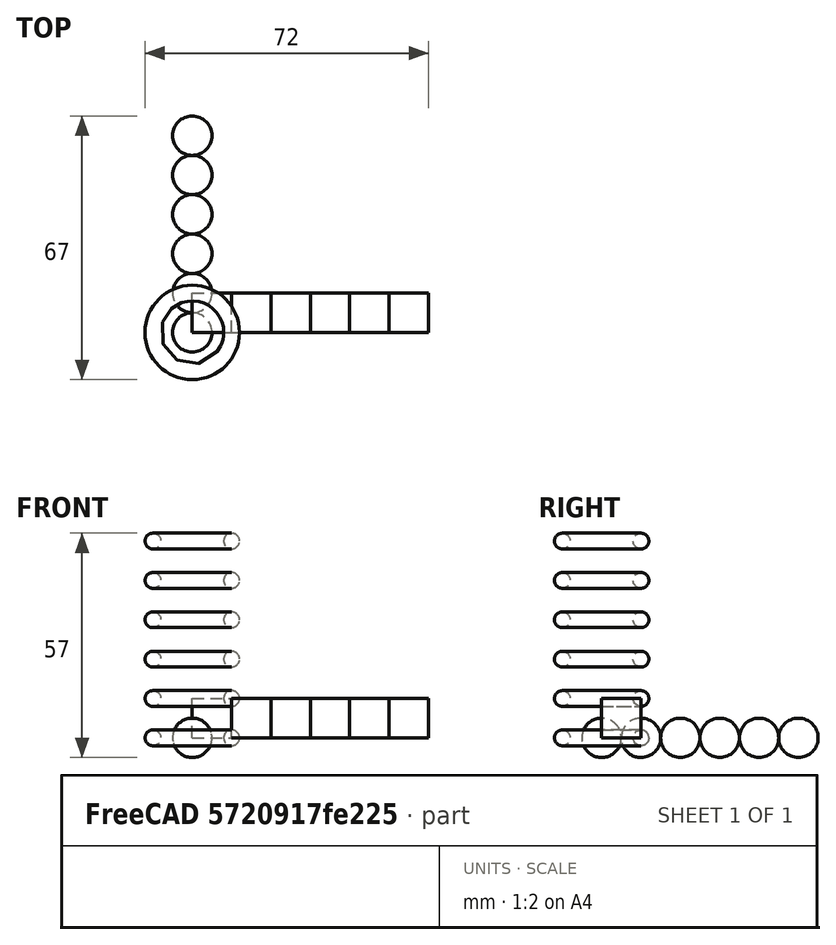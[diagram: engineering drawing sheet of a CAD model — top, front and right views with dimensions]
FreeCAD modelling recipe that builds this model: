
FCSTD DOCUMENT  (FreeCAD 0.18R16110 (Git))
Label: basic_shapes
License: All rights reserved
LicenseURL: http://en.wikipedia.org/wiki/All_rights_reserved
objects: App::Part×9, Part::Box×8, Part::Sphere×8, Part::Torus×8
note: 24 computed .brp shape members not serialized (recipe doc carries the construction recipe); baked Part::Feature solids carry a one-line shape summary decoded from their .brp

FEATURE [Part::Box] Box  label="Cube_1_1"
  AttacherType = Attacher::AttachEngine3D
  Height = 10
  Length = 10
  Width = 10
FEATURE [Part::Sphere] Sphere  label="Sphere_1_2"
  Angle1 = -90
  Angle2 = 90
  Angle3 = 360
  AttacherType = Attacher::AttachEngine3D
  Radius = 5
FEATURE [Part::Torus] Torus  label="Torus_1_3"
  Angle1 = -180
  Angle2 = 180
  Angle3 = 360
  AttacherType = Attacher::AttachEngine3D
  Radius1 = 10
  Radius2 = 2
FEATURE [App::Part] Part  label="Assembly_1"
  Group = -> [Box,Sphere,Torus]
  Origin = -> Origin
FEATURE [Part::Box] Box001  label="Cube_2_1"
  AttacherType = Attacher::AttachEngine3D
  Height = 10
  Length = 10
  Placement = pos=(10,0,0) rot=(0,0,1;0rad)
  Width = 10
FEATURE [Part::Sphere] Sphere001  label="Sphere_2_2"
  Angle1 = -90
  Angle2 = 90
  Angle3 = 360
  AttacherType = Attacher::AttachEngine3D
  Placement = pos=(0,10,0) rot=(0,0,1;0rad)
  Radius = 5
FEATURE [Part::Torus] Torus001  label="Torus_2_3"
  Angle1 = -180
  Angle2 = 180
  Angle3 = 360
  AttacherType = Attacher::AttachEngine3D
  Placement = pos=(0,0,10) rot=(0,0,1;0rad)
  Radius1 = 10
  Radius2 = 2
FEATURE [Part::Box] Box002  label="Cube_3_1"
  AttacherType = Attacher::AttachEngine3D
  Height = 10
  Length = 10
  Placement = pos=(30,0,0) rot=(0,0,1;0rad)
  Width = 10
FEATURE [Part::Torus] Torus002  label="Torus_3_2"
  Angle1 = -180
  Angle2 = 180
  Angle3 = 360
  AttacherType = Attacher::AttachEngine3D
  Placement = pos=(0,0,30) rot=(0,0,1;0rad)
  Radius1 = 10
  Radius2 = 2
FEATURE [Part::Sphere] Sphere002  label="Sphere_3_3"
  Angle1 = -90
  Angle2 = 90
  Angle3 = 360
  AttacherType = Attacher::AttachEngine3D
  Placement = pos=(0,30,0) rot=(0,0,1;0rad)
  Radius = 5
FEATURE [Part::Box] Box003  label="Cube_2_4_1"
  AttacherType = Attacher::AttachEngine3D
  Height = 10
  Length = 10
  Placement = pos=(20,0,0) rot=(0,0,1;0rad)
  Width = 10
FEATURE [Part::Torus] Torus003  label="Torus_2_4_2"
  Angle1 = -180
  Angle2 = 180
  Angle3 = 360
  AttacherType = Attacher::AttachEngine3D
  Placement = pos=(0,0,20) rot=(0,0,1;0rad)
  Radius1 = 10
  Radius2 = 2
FEATURE [Part::Sphere] Sphere003  label="Sphere_2_4_3"
  Angle1 = -90
  Angle2 = 90
  Angle3 = 360
  AttacherType = Attacher::AttachEngine3D
  Placement = pos=(0,20,0) rot=(0,0,1;0rad)
  Radius = 5
FEATURE [App::Part] Part003  label="Assembly_2_4"
  Group = -> [Box003,Torus003,Sphere003]
  Origin = -> Origin003
FEATURE [App::Part] Part001  label="Assembly_2"
  Group = -> [Box001,Sphere001,Torus001,Part003]
  Origin = -> Origin001
FEATURE [Part::Box] Box004  label="Cube_3_4_1_1"
  AttacherType = Attacher::AttachEngine3D
  Height = 10
  Length = 10
  Placement = pos=(40,0,0) rot=(0,0,1;0rad)
  Width = 10
FEATURE [Part::Sphere] Sphere004  label="Sphere_3_4_1_2"
  Angle1 = -90
  Angle2 = 90
  Angle3 = 360
  AttacherType = Attacher::AttachEngine3D
  Placement = pos=(0,40,0) rot=(0,0,1;0rad)
  Radius = 5
FEATURE [Part::Torus] Torus004  label="Torus_3_4_1_3"
  Angle1 = -180
  Angle2 = 180
  Angle3 = 360
  AttacherType = Attacher::AttachEngine3D
  Placement = pos=(0,0,40) rot=(0,0,1;0rad)
  Radius1 = 10
  Radius2 = 2
FEATURE [App::Part] Part005  label="Assembly_3_4_1"
  Group = -> [Box004,Sphere004,Torus004]
  Origin = -> Origin005
FEATURE [App::Part] Part004  label="Assembly_3_4"
  Group = -> [Part005]
  Origin = -> Origin004
FEATURE [App::Part] Part002  label="Assembly_3"
  Group = -> [Box002,Torus002,Sphere002,Part004]
  Origin = -> Origin002
FEATURE [Part::Box] Box005  label="Cube_4"
  AttacherType = Attacher::AttachEngine3D
  Height = 10
  Length = 10
  Placement = pos=(50,0,0) rot=(0,0,1;0rad)
  Width = 10
FEATURE [Part::Sphere] Sphere005  label="Sphere_5"
  Angle1 = -90
  Angle2 = 90
  Angle3 = 360
  AttacherType = Attacher::AttachEngine3D
  Placement = pos=(0,50,0) rot=(0,0,1;0rad)
  Radius = 5
FEATURE [Part::Torus] Torus005  label="Torus_6"
  Angle1 = -180
  Angle2 = 180
  Angle3 = 360
  AttacherType = Attacher::AttachEngine3D
  Placement = pos=(0,0,50) rot=(0,0,1;0rad)
  Radius1 = 10
  Radius2 = 2
FEATURE [Part::Box] Box006  label="Cube_7_1_1"
  AttacherType = Attacher::AttachEngine3D
  Height = 10
  Length = 10
  Width = 10
FEATURE [Part::Torus] Torus006  label="Torus_7_1_2"
  Angle1 = -180
  Angle2 = 180
  Angle3 = 360
  AttacherType = Attacher::AttachEngine3D
  Radius1 = 10
  Radius2 = 2
FEATURE [Part::Sphere] Sphere006  label="Sphere_7_1_3"
  Angle1 = -90
  Angle2 = 90
  Angle3 = 360
  AttacherType = Attacher::AttachEngine3D
  Radius = 5
FEATURE [App::Part] Part007  label="Assembly_7_1"
  Group = -> [Box006,Torus006,Sphere006]
  Origin = -> Origin007
  Placement = pos=(30,30,30) rot=(0,0,1;0rad)
FEATURE [Part::Box] Box007  label="Cube_7_2_1"
  AttacherType = Attacher::AttachEngine3D
  Height = 10
  Length = 10
  Placement = pos=(10,0,0) rot=(0,0,1;0rad)
  Width = 10
FEATURE [Part::Torus] Torus007  label="Torus_7_2_2"
  Angle1 = -180
  Angle2 = 180
  Angle3 = 360
  AttacherType = Attacher::AttachEngine3D
  Placement = pos=(0,0,10) rot=(0,0,1;0rad)
  Radius1 = 10
  Radius2 = 2
FEATURE [Part::Sphere] Sphere007  label="Sphere_7_2_3"
  Angle1 = -90
  Angle2 = 90
  Angle3 = 360
  AttacherType = Attacher::AttachEngine3D
  Placement = pos=(0,10,0) rot=(0,0,1;0rad)
  Radius = 5
FEATURE [App::Part] Part008  label="Assembly_7_2"
  Group = -> [Box007,Torus007,Sphere007]
  Origin = -> Origin008
  Placement = pos=(30,30,30) rot=(0,0,1;0rad)
FEATURE [App::Part] Part006  label="Assembly_7"
  Group = -> [Part007,Part008]
  Origin = -> Origin006
